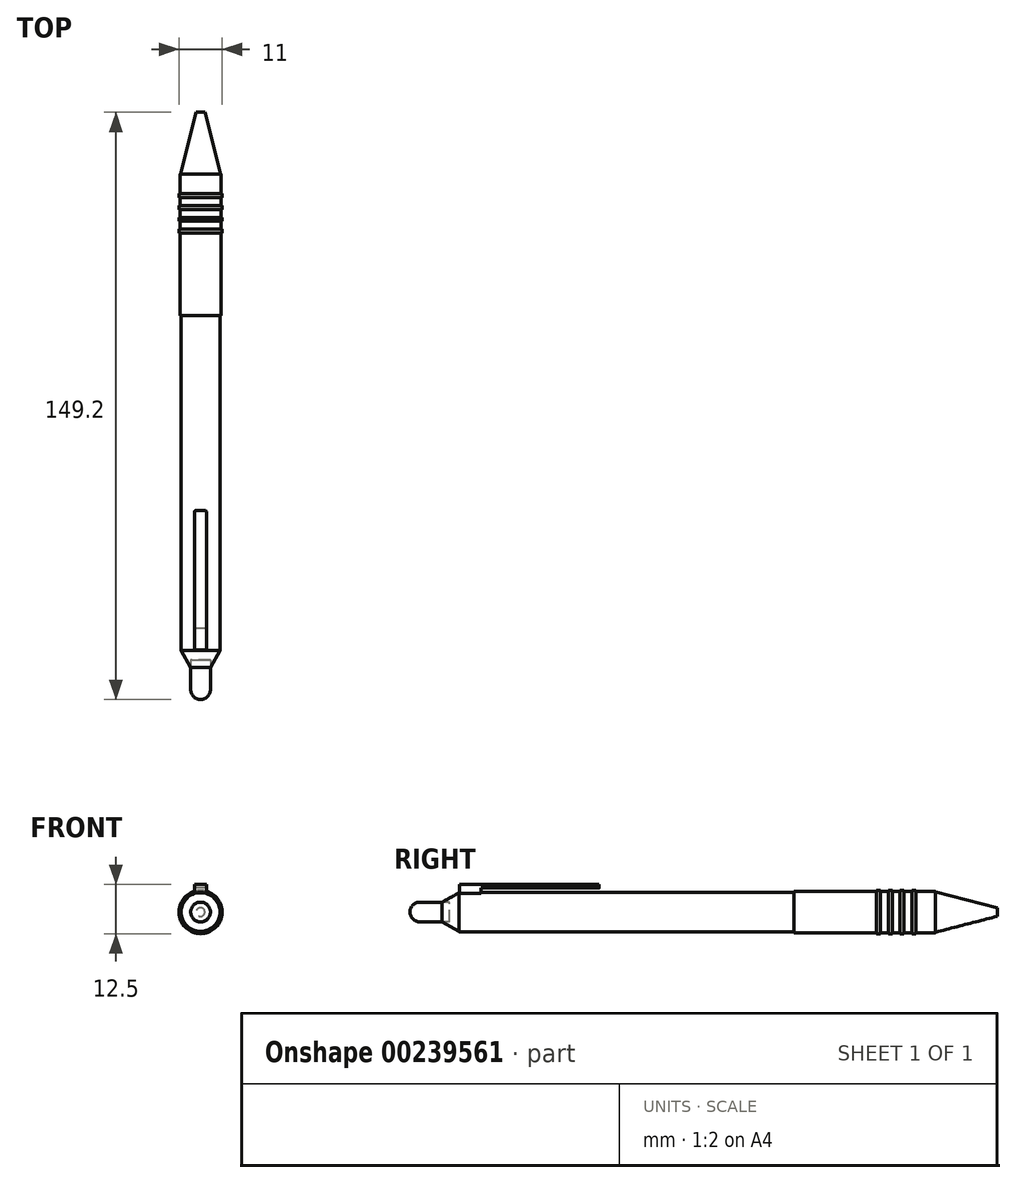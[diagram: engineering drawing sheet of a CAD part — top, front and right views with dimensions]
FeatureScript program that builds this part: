
annotation { "Feature Type Name" : "Feature", "Feature Type Description" : "" }
export const myFeature = defineFeature(function(context is Context, id is Id, definition is map)
    precondition{}
    {
        {
            var Q0;
            Q0=qCreatedBy(makeId("Front.planeOp"),FACE);
            var sketch = newSketch(context, id + "F0", { "sketchPlane" : qUnion([Q0])});
            skArc(sketch, "E0", {"start": v(0, -2.5) * mm, "mid": v(2.5, 0) * mm, "end": v(0, 2.5) * mm});
            skLineSegment(sketch, "E1", {"start": v(0, 2.5) * mm, "end": v(0, -2.5) * mm});
            skSolve(sketch);
        }
        {
            var Q0;
            Q0 = qSketchRegion(id + "F0", true);
            var Q1;
            Q1=sQuery(id+"F0.wireOp",EDGE,"E1");
            revolve(context, id + "F1", {"entities" : qUnion([Q0]), "axis" : qUnion([Q1]), "revolveType" : RevolveType.FULL});
        }
        {
            var Q0;
            Q0=qCreatedBy(makeId("Front.planeOp"),FACE);
            var sketch = newSketch(context, id + "F2", { "sketchPlane" : qUnion([Q0])});
            skLineSegment(sketch, "E2.bottom", {"start": v(0, 2.54) * mm, "end": v(-2.7, 2.54) * mm});
            skLineSegment(sketch, "E2.top", {"start": v(0, -2.58) * mm, "end": v(-2.7, -2.58) * mm});
            skLineSegment(sketch, "E2.left", {"start": v(0, 2.54) * mm, "end": v(0, -2.58) * mm});
            skLineSegment(sketch, "E2.right", {"start": v(-2.7, 2.54) * mm, "end": v(-2.7, -2.58) * mm});
            skSolve(sketch);
        }
        {
            var Q0;
            Q0 = qSketchRegion(id + "F2", true);
            extrude(context, id + "F3", {"entities" : qUnion([Q0]), "operationType" : NewBodyOperationType.REMOVE, "endBound" : BoundingType.THROUGH_ALL, "oppositeDirection" : true, "depth" : 25 * mm});
        }
        {
            var Q0;
            Q0=makeQuery(id+"F3.boolean.opBoolean","COPY",FACE,{"derivedFrom":makeQuery(id+"F3.opExtrude","SWEPT_FACE",FACE,{"disambiguationData":[OSD([sQuery(id+"F2.wireOp",EDGE,"E2.left")])]})});
            var sketch = newSketch(context, id + "F4", { "sketchPlane" : qUnion([Q0])});
            skLineSegment(sketch, "E3.bottom", {"start": v(0, 2.5) * mm, "end": v(-2.64, 2.5) * mm});
            skLineSegment(sketch, "E3.top", {"start": v(0, -2.5) * mm, "end": v(-2.64, -2.5) * mm});
            skLineSegment(sketch, "E3.left", {"start": v(0, 2.5) * mm, "end": v(0, -2.5) * mm});
            skLineSegment(sketch, "E3.right", {"start": v(-2.64, 2.5) * mm, "end": v(-2.64, -2.5) * mm});
            skSolve(sketch);
        }
        {
            var Q0;
            Q0 = qSketchRegion(id + "F4", true);
            extrude(context, id + "F5", {"entities" : qUnion([Q0]), "operationType" : NewBodyOperationType.REMOVE, "endBound" : BoundingType.THROUGH_ALL, "oppositeDirection" : true, "depth" : 25 * mm});
        }
        {
            var Q0;
            Q0=makeQuery(id+"F5.boolean.opBoolean","MERGE",FACE,{"derivedFrom":[makeQuery(id+"F3.boolean.opBoolean","COPY",FACE,{"derivedFrom":makeQuery(id+"F3.opExtrude","CAP_FACE",FACE,{"disambiguationData":[OSD([sQuery(id+"F2.wireOp",EDGE,"E2.bottom"),sQuery(id+"F2.wireOp",EDGE,"E2.top"),sQuery(id+"F2.wireOp",EDGE,"E2.left"),sQuery(id+"F2.wireOp",EDGE,"E2.right")])],"isStart":true})}),makeQuery(id+"F5.opExtrude","SWEPT_FACE",FACE,{"disambiguationData":[OSD([sQuery(id+"F4.wireOp",EDGE,"E3.left")])]})]});
            var sketch = newSketch(context, id + "F6", { "sketchPlane" : qUnion([Q0])});
            skCircle(sketch, "E4", {"center": v(0, 0) * mm, "radius": 2.5 * mm});
            skSolve(sketch);
        }
        {
            var Q0;
            Q0 = qSketchRegion(id + "F6", true);
            extrude(context, id + "F7", {"entities" : qUnion([Q0]), "operationType" : NewBodyOperationType.ADD, "depth" : 10 * mm});
        }
        {
            var Q0;
            Q0=makeQuery(id+"F7.opExtrude","CAP_FACE",FACE,{"disambiguationData":[OSD([sQuery(id+"F6.wireOp",EDGE,"E4")])],"isStart":false});
            var sketch = newSketch(context, id + "F8", { "sketchPlane" : qUnion([Q0])});
            skCircle(sketch, "E5", {"center": v(0, 0) * mm, "radius": 5 * mm});
            skSolve(sketch);
        }
        {
            var Q0;
            Q0 = qSketchRegion(id + "F8", true);
            extrude(context, id + "F9", {"entities" : qUnion([Q0]), "operationType" : NewBodyOperationType.ADD, "depth" : 85 * mm});
        }
        {
            var Q0;
            Q0=makeQuery(id+"F9.opExtrude","CAP_FACE",FACE,{"disambiguationData":[OSD([sQuery(id+"F8.wireOp",EDGE,"E5")])],"isStart":false});
            var sketch = newSketch(context, id + "F10", { "sketchPlane" : qUnion([Q0])});
            skCircle(sketch, "E6", {"center": v(0, 0) * mm, "radius": 5.25 * mm});
            skSolve(sketch);
        }
        {
            var Q0;
            Q0 = qSketchRegion(id + "F10", true);
            extrude(context, id + "F11", {"entities" : qUnion([Q0]), "operationType" : NewBodyOperationType.ADD, "depth" : 21 * mm});
        }
        {
            var Q0;
            Q0=makeQuery(id+"F11.opExtrude","CAP_FACE",FACE,{"disambiguationData":[OSD([sQuery(id+"F10.wireOp",EDGE,"E6")])],"isStart":false});
            var sketch = newSketch(context, id + "F12", { "sketchPlane" : qUnion([Q0])});
            skCircle(sketch, "E7", {"center": v(0, 0) * mm, "radius": 5.5 * mm});
            skSolve(sketch);
        }
        {
            var Q0;
            Q0 = qSketchRegion(id + "F12", true);
            extrude(context, id + "F13", {"entities" : qUnion([Q0]), "operationType" : NewBodyOperationType.ADD, "depth" : 1 * mm});
        }
        {
            var Q0;
            Q0=makeQuery(id+"F13.opExtrude","CAP_FACE",FACE,{"disambiguationData":[OSD([sQuery(id+"F12.wireOp",EDGE,"E7")])],"isStart":false});
            var sketch = newSketch(context, id + "F14", { "sketchPlane" : qUnion([Q0])});
            skCircle(sketch, "E8", {"center": v(0, 0) * mm, "radius": 5.25 * mm});
            skSolve(sketch);
        }
        {
            var Q0;
            Q0 = qSketchRegion(id + "F14", true);
            extrude(context, id + "F15", {"entities" : qUnion([Q0]), "operationType" : NewBodyOperationType.ADD, "depth" : 2 * mm});
        }
        {
            var Q0;
            Q0=makeQuery(id+"F15.opExtrude","CAP_FACE",FACE,{"disambiguationData":[OSD([sQuery(id+"F14.wireOp",EDGE,"E8")])],"isStart":false});
            var sketch = newSketch(context, id + "F16", { "sketchPlane" : qUnion([Q0])});
            skCircle(sketch, "E9", {"center": v(0, 0) * mm, "radius": 5.5 * mm});
            skSolve(sketch);
        }
        {
            var Q0;
            Q0 = qSketchRegion(id + "F16", true);
            extrude(context, id + "F17", {"entities" : qUnion([Q0]), "operationType" : NewBodyOperationType.ADD, "depth" : 1 * mm});
        }
        {
            var Q0;
            Q0=makeQuery(id+"F17.opExtrude","CAP_FACE",FACE,{"disambiguationData":[OSD([sQuery(id+"F16.wireOp",EDGE,"E9")])],"isStart":false});
            var sketch = newSketch(context, id + "F18", { "sketchPlane" : qUnion([Q0])});
            skCircle(sketch, "E10", {"center": v(0, 0) * mm, "radius": 5.25 * mm});
            skSolve(sketch);
        }
        {
            var Q0;
            Q0 = qSketchRegion(id + "F18", true);
            extrude(context, id + "F19", {"entities" : qUnion([Q0]), "operationType" : NewBodyOperationType.ADD, "depth" : 2 * mm});
        }
        {
            var Q0;
            Q0=makeQuery(id+"F19.opExtrude","CAP_FACE",FACE,{"disambiguationData":[OSD([sQuery(id+"F18.wireOp",EDGE,"E10")])],"isStart":false});
            var sketch = newSketch(context, id + "F20", { "sketchPlane" : qUnion([Q0])});
            skCircle(sketch, "E11", {"center": v(0, 0) * mm, "radius": 5.5 * mm});
            skSolve(sketch);
        }
        {
            var Q0;
            Q0 = qSketchRegion(id + "F20", true);
            extrude(context, id + "F21", {"entities" : qUnion([Q0]), "operationType" : NewBodyOperationType.ADD, "depth" : 1 * mm});
        }
        {
            var Q0;
            Q0=makeQuery(id+"F21.opExtrude","CAP_FACE",FACE,{"disambiguationData":[OSD([sQuery(id+"F20.wireOp",EDGE,"E11")])],"isStart":false});
            var sketch = newSketch(context, id + "F22", { "sketchPlane" : qUnion([Q0])});
            skCircle(sketch, "E12", {"center": v(0, 0) * mm, "radius": 5.25 * mm});
            skSolve(sketch);
        }
        {
            var Q0;
            Q0 = qSketchRegion(id + "F22", true);
            extrude(context, id + "F23", {"entities" : qUnion([Q0]), "operationType" : NewBodyOperationType.ADD, "depth" : 2 * mm});
        }
        {
            var Q0;
            Q0=makeQuery(id+"F23.opExtrude","CAP_FACE",FACE,{"disambiguationData":[OSD([sQuery(id+"F22.wireOp",EDGE,"E12")])],"isStart":false});
            var sketch = newSketch(context, id + "F24", { "sketchPlane" : qUnion([Q0])});
            skCircle(sketch, "E13", {"center": v(0, 0) * mm, "radius": 5.5 * mm});
            skSolve(sketch);
        }
        {
            var Q0;
            Q0 = qSketchRegion(id + "F24", true);
            extrude(context, id + "F25", {"entities" : qUnion([Q0]), "operationType" : NewBodyOperationType.ADD, "depth" : 1 * mm});
        }
        {
            var Q0;
            Q0=makeQuery(id+"F25.opExtrude","CAP_FACE",FACE,{"disambiguationData":[OSD([sQuery(id+"F24.wireOp",EDGE,"E13")])],"isStart":false});
            var sketch = newSketch(context, id + "F26", { "sketchPlane" : qUnion([Q0])});
            skCircle(sketch, "E14", {"center": v(0, 0) * mm, "radius": 5.25 * mm});
            skSolve(sketch);
        }
        {
            var Q0;
            Q0 = qSketchRegion(id + "F26", true);
            extrude(context, id + "F27", {"entities" : qUnion([Q0]), "operationType" : NewBodyOperationType.ADD, "depth" : 5 * mm});
        }
        {
            var Q0;
            Q0=qCreatedBy(makeId("Top.planeOp"),FACE);
            var sketch = newSketch(context, id + "F28", { "sketchPlane" : qUnion([Q0])});
            skLineSegment(sketch, "E15.bottom", {"start": v(1.55, 10.05) * mm, "end": v(-1.55, 10.05) * mm});
            skLineSegment(sketch, "E15.top", {"start": v(1.55, 15.56) * mm, "end": v(-1.55, 15.56) * mm});
            skLineSegment(sketch, "E15.left", {"start": v(1.55, 10.05) * mm, "end": v(1.55, 15.56) * mm});
            skLineSegment(sketch, "E15.right", {"start": v(-1.55, 10.05) * mm, "end": v(-1.55, 15.56) * mm});
            skSolve(sketch);
        }
        {
            var Q0;
            Q0 = qSketchRegion(id + "F28", true);
            extrude(context, id + "F29", {"entities" : qUnion([Q0]), "operationType" : NewBodyOperationType.ADD, "depth" : 7 * mm});
        }
        {
            var Q0;
            Q0=makeQuery(id+"F29.opExtrude","SWEPT_FACE",FACE,{"disambiguationData":[OSD([sQuery(id+"F28.wireOp",EDGE,"E15.top")])]});
            var sketch = newSketch(context, id + "F30", { "sketchPlane" : qUnion([Q0])});
            skLineSegment(sketch, "E16.bottom", {"start": v(-1.55, 7) * mm, "end": v(1.55, 7) * mm});
            skLineSegment(sketch, "E16.top", {"start": v(-1.55, 6.12) * mm, "end": v(1.55, 6.12) * mm});
            skLineSegment(sketch, "E16.left", {"start": v(-1.55, 7) * mm, "end": v(-1.55, 6.12) * mm});
            skLineSegment(sketch, "E16.right", {"start": v(1.55, 7) * mm, "end": v(1.55, 6.12) * mm});
            skSolve(sketch);
        }
        {
            var Q0;
            Q0 = qSketchRegion(id + "F30", true);
            extrude(context, id + "F31", {"entities" : qUnion([Q0]), "operationType" : NewBodyOperationType.ADD, "depth" : 30 * mm});
        }
        {
            var Q0;
            Q0=qCreatedBy(makeId("Right.planeOp"),FACE);
            var sketch = newSketch(context, id + "F32", { "sketchPlane" : qUnion([Q0])});
            skLineSegment(sketch, "E17", {"start": v(5.69, -2.5) * mm, "end": v(10.05, -4.95) * mm});
            skLineSegment(sketch, "E18", {"start": v(10.05, -4.95) * mm, "end": v(10.05, -2.49) * mm});
            skLineSegment(sketch, "E19", {"start": v(10.05, -2.49) * mm, "end": v(5.69, -2.5) * mm});
            skSolve(sketch);
        }
        {
            var Q0;
            Q0 = qSketchRegion(id + "F32", true);
            var Q1;
            Q1=makeQuery(id+"F7.opExtrude","SWEPT_FACE",FACE,{"disambiguationData":[OSD([sQuery(id+"F6.wireOp",EDGE,"E4")])]});
            revolve(context, id + "F33", {"operationType" : NewBodyOperationType.ADD, "entities" : qUnion([Q0]), "axis" : qUnion([Q1]), "revolveType" : RevolveType.FULL});
        }
        {
            var Q0;
            Q0=qCreatedBy(makeId("Right.planeOp"),FACE);
            var sketch = newSketch(context, id + "F34", { "sketchPlane" : qUnion([Q0])});
            skLineSegment(sketch, "E20", {"start": v(130.97, 0) * mm, "end": v(130.97, -5.13) * mm});
            skLineSegment(sketch, "E21", {"start": v(130.97, 0) * mm, "end": v(150.97, 0) * mm});
            skLineSegment(sketch, "E22", {"start": v(150.97, 0) * mm, "end": v(130.97, -5.13) * mm});
            skSolve(sketch);
        }
        {
            var Q0;
            Q0 = qSketchRegion(id + "F34", true);
            var Q1;
            Q1=sQuery(id+"F34.wireOp",EDGE,"E21");
            revolve(context, id + "F35", {"operationType" : NewBodyOperationType.ADD, "entities" : qUnion([Q0]), "axis" : qUnion([Q1]), "revolveType" : RevolveType.FULL});
        }
        {
            var Q0;
            Q0=qCreatedBy(makeId("Right.planeOp"),FACE);
            var sketch = newSketch(context, id + "F36", { "sketchPlane" : qUnion([Q0])});
            skLineSegment(sketch, "E23.bottom", {"start": v(146.7, 1.31) * mm, "end": v(151.36, 1.31) * mm});
            skLineSegment(sketch, "E23.top", {"start": v(146.7, -1.8) * mm, "end": v(151.36, -1.8) * mm});
            skLineSegment(sketch, "E23.left", {"start": v(146.7, 1.31) * mm, "end": v(146.7, -1.8) * mm});
            skLineSegment(sketch, "E23.right", {"start": v(151.36, 1.31) * mm, "end": v(151.36, -1.8) * mm});
            skSolve(sketch);
        }
        {
            var Q0;
            Q0 = qSketchRegion(id + "F36", true);
            extrude(context, id + "F37", {"entities" : qUnion([Q0]), "operationType" : NewBodyOperationType.REMOVE, "endBound" : BoundingType.THROUGH_ALL, "oppositeDirection" : true, "depth" : 50 * mm});
        }
        {
            var Q0;
            Q0=makeQuery(id+"F37.boolean.opBoolean","COPY",FACE,{"derivedFrom":makeQuery(id+"F37.opExtrude","CAP_FACE",FACE,{"disambiguationData":[OSD([sQuery(id+"F36.wireOp",EDGE,"E23.bottom"),sQuery(id+"F36.wireOp",EDGE,"E23.top"),sQuery(id+"F36.wireOp",EDGE,"E23.left"),sQuery(id+"F36.wireOp",EDGE,"E23.right")])],"isStart":true})});
            var sketch = newSketch(context, id + "F38", { "sketchPlane" : qUnion([Q0])});
            skLineSegment(sketch, "E24.bottom", {"start": v(-146.7, 1.1) * mm, "end": v(-151.14, 1.1) * mm});
            skLineSegment(sketch, "E24.top", {"start": v(-146.7, -1.2) * mm, "end": v(-151.14, -1.2) * mm});
            skLineSegment(sketch, "E24.left", {"start": v(-146.7, 1.1) * mm, "end": v(-146.7, -1.2) * mm});
            skLineSegment(sketch, "E24.right", {"start": v(-151.14, 1.1) * mm, "end": v(-151.14, -1.2) * mm});
            skSolve(sketch);
        }
        {
            var Q0;
            Q0 = qSketchRegion(id + "F38", true);
            extrude(context, id + "F39", {"entities" : qUnion([Q0]), "operationType" : NewBodyOperationType.REMOVE, "endBound" : BoundingType.THROUGH_ALL, "oppositeDirection" : true, "depth" : 25 * mm});
        }
        {
            var Q0;
            Q0=makeQuery(id+"F31.opExtrude","CAP_EDGE",EDGE,{"disambiguationData":[OSD([sQuery(id+"F30.wireOp",EDGE,"E16.right")])],"isStart":false});
            fillet(context, id + "F40", {"entities" : qUnion([Q0]), "radius" : 0.5 * mm, "tangentPropagation" : true, "allowEdgeOverflow" : false});
        }
        {
            var Q0;
            Q0=makeQuery(id+"F31.opExtrude","CAP_EDGE",EDGE,{"disambiguationData":[OSD([sQuery(id+"F30.wireOp",EDGE,"E16.left")])],"isStart":false});
            fillet(context, id + "F41", {"entities" : qUnion([Q0]), "radius" : 0.5 * mm, "tangentPropagation" : true, "allowEdgeOverflow" : false});
        }
    });
